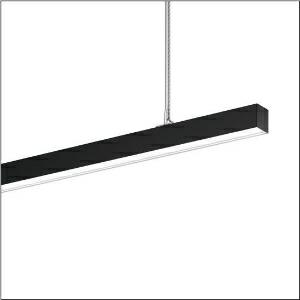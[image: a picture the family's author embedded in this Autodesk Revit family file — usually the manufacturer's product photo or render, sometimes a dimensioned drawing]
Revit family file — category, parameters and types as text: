
# Revit family: silica_r__21_51mx30db35bb_2e66
name_source: partatom
category: Lighting Fixtures
units: mm (PartAtom-declared; Revit-internal decimal feet)

## family parameters
Cut with Voids When Loaded = No
Host = Face
Light Source = No
Part Type = Normal
Room Calculation Point = No
Round Connector Dimension = Use Diameter
Shared = No

## types (1)
- --- (1 x LED, 5260 lm, 34.1 W, 3000K)
    Apparent Load = 34 VA
    CIE Flux Codes = 47 79 96 57 100
    Color Rendering = 80
    Color Temperature = 3000K
    Default Elevation = 1800 mm
    Description = Silica® 21, office luminaire, primary optical cover: cover, of PMMA, opal, light emission: direct/indirect distribution, primary light characteristic: symmetric, installation type: suspended mounting, LED, rated luminous flux: 5.260lm, luminous efficacy: 154lm/W, light colour: 830, colour temperature: 3000K, with terminal, 3+2-pole, max. 2.5mm², mains connection: 220..240V, AC, 50/60Hz, rated input power: 34.1W, luminaire housing, of aluminium, jet black (RAL 9005), length: 1.504mm, width: 53mm, height: 53mm, protection rating (complete): IP20, insulation class (complete): insulation class I (protective earthing), certification: CE, permissible operating ambient temperature: 0..+35°C, standard: EN 50419, packaging unit: 1 piece
    Height = 53 mm
    Lamp = 1 x LED
    Lamp Light Flux = 5260 lm
    Lamp Power = 34.1 W
    Lamp count = 1
    Length = 1504 mm
    Luminous efficacy = 154 lm/W
    Manufacturer = Siteco
    ModVariant = No
    Model = 51MX30DB35BB
    Mounting Place = Ceiling
    Mounting Type = Pendant
    Number of Poles = 1
    OnlyDefault = Yes
    Power Factor = 1
    Product Name = Silica® 21
    Product group = office luminaire | ceiling pendant
    ProductGroupID = 905
    Protection Class = Protection class I
    Protection Degree = IP 20
    RLX_Detail_Level = 1
    RlxData = <blob elided: 26153 chars, md5=6580e5ba>
    Socket = socket
    Standby Power = 0 W
    System Light Flux = 5260 lm
    System Power = 34 W
    Type Comments = factory setting: luminous flux: 100 % | dim-lin: 254 | 233 mA
    Type Image = l_1251735.jpg
    URL = http://relux.com
    VarID = @adj_025381
    Voltage = 0 V
    Weight = 0.00 kg
    Width = 53 mm

## geometry (parser evidence)
native form markers: Blend x4, Sweep x13
no freeform markers — native parametric forms only
